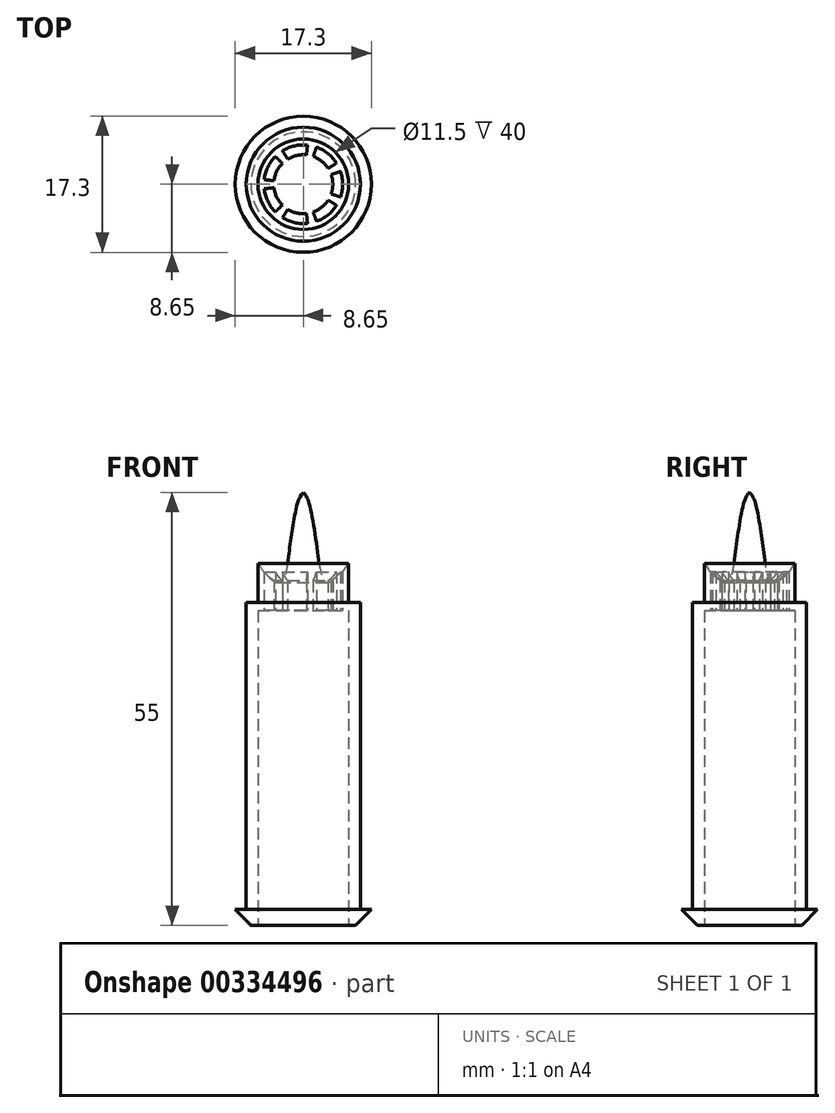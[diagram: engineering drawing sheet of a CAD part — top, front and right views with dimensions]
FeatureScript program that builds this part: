
annotation { "Feature Type Name" : "Feature", "Feature Type Description" : "" }
export const myFeature = defineFeature(function(context is Context, id is Id, definition is map)
    precondition{}
    {
        {
            var Q0;
            Q0=qCreatedBy(makeId("Front.planeOp"),FACE);
            var sketch = newSketch(context, id + "F0", { "sketchPlane" : qUnion([Q0])});
            skLineSegment(sketch, "E0", {"start": v(0, 0) * mm, "end": v(0, 55.6) * mm});
            skLineSegment(sketch, "E1.0", {"start": v(7.25, 2) * mm, "end": v(7.25, 41) * mm});
            skLineSegment(sketch, "E2.0", {"start": v(5.75, 5) * mm, "end": v(5.75, 38) * mm});
            skLineSegment(sketch, "E3.0", {"start": v(8.65, 0) * mm, "end": v(8.65, 2) * mm});
            skLineSegment(sketch, "E4.0", {"start": v(7.25, 2) * mm, "end": v(8.65, 2) * mm});
            skLineSegment(sketch, "E5", {"start": v(5.75, 0) * mm, "end": v(8.65, 0) * mm});
            skLineSegment(sketch, "E6.0", {"start": v(4.75, 40) * mm, "end": v(5.75, 40) * mm});
            skArc(sketch, "E7", {"start": v(5.75, 38) * mm, "mid": v(5.46, 38.7) * mm, "end": v(4.75, 39) * mm});
            skLineSegment(sketch, "E8.trimOffspring", {"start": v(5.75, 40) * mm, "end": v(5.75, 41) * mm});
            skLineSegment(sketch, "E9", {"start": v(4.75, 40) * mm, "end": v(4.75, 39) * mm});
            skPoint(sketch, "E10.endSnap0", {"position": v(5.75, 21.5) * mm});
            skLineSegment(sketch, "E11.MirrorCS", {"start": v(4.75, 3) * mm, "end": v(5.75, 3) * mm});
            skLineSegment(sketch, "E12.MirrorCS", {"start": v(4.75, 3) * mm, "end": v(4.75, 4) * mm});
            skArc(sketch, "E13.MirrorCS", {"start": v(5.75, 5) * mm, "mid": v(5.46, 4.3) * mm, "end": v(4.75, 4) * mm});
            skLineSegment(sketch, "E14", {"start": v(5.75, 3) * mm, "end": v(5.75, 0) * mm});
            skLineSegment(sketch, "E15.0", {"start": v(5.75, 41) * mm, "end": v(7.25, 41) * mm});
            skSolve(sketch);
        }
        {
            var Q0;
            Q0=qSketchRegion(id+"F0",true);
            var Q1;
            Q1=sQuery(id+"F0.wireOp",EDGE,"E0");
            revolve(context, id + "F1", {"entities" : qUnion([Q0]), "axis" : qUnion([Q1]), "revolveType" : RevolveType.FULL});
        }
        {
            var Q0;
            Q0=makeQuery(id+"F1.opRevolve","SWEPT_EDGE",EDGE,{"disambiguationData":[OSD([sQuery(id+"F0.wireOp",EDGE,"E3.0"),sQuery(id+"F0.wireOp",EDGE,"E5")])]});
            chamfer(context, id + "F2", {"entities" : qUnion([Q0]), "chamferType" : ChamferType.TWO_OFFSETS, "width1" : 2 * mm, "oppositeDirection" : false, "width2" : 2 * mm, "tangentPropagation" : true});
        }
        {
            var Q0;
            Q0=qCreatedBy(makeId("Front.planeOp"),FACE);
            var sketch = newSketch(context, id + "F3", { "sketchPlane" : qUnion([Q0])});
            skLineSegment(sketch, "E16", {"start": v(0, 41) * mm, "end": v(0, 55) * mm});
            skLineSegment(sketch, "E17", {"start": v(5.75, 40) * mm, "end": v(5.75, 46) * mm});
            skFitSpline(sketch, "E18", {"points": [v(0, 55) * mm, v(0.35, 54.58) * mm, v(0.8, 53.42) * mm, v(1.77, 47.7) * mm, v(2.42, 44.16) * mm, v(3.02, 43.55) * mm, v(4.25, 44.14) * mm, v(5.17, 45.15) * mm, v(5.75, 46) * mm], "startDerivative": vector(6.12, -4.44) * mm, "endDerivative": vector(6.63, 7.2) * mm});
            skLineSegment(sketch, "E19.0.0", {"start": v(-5.75, 40) * mm, "end": v(5.75, 40) * mm});
            skLineSegment(sketch, "E20", {"start": v(0, 41) * mm, "end": v(0, 39.56) * mm});
            skPoint(sketch, "E20.endSnap0", {"position": v(0, 40) * mm});
            skPoint(sketch, "E21.orphan", {"position": v(5.75, 41) * mm});
            skSolve(sketch);
        }
        {
            var Q0;
            Q0 = qSketchRegion(id + "F3", true);
            var Q1;
            Q1=makeQuery(id+"F1.opRevolve","SWEPT_FACE",FACE,{"disambiguationData":[OSD([sQuery(id+"F0.wireOp",EDGE,"E1.0")])]});
            revolve(context, id + "F4", {"operationType" : NewBodyOperationType.ADD, "surfaceOperationType" : NewSurfaceOperationType.NEW, "entities" : qUnion([Q0]), "axis" : qUnion([Q1]), "revolveType" : RevolveType.FULL});
        }
        {
            var Q0;
            Q0=makeQuery(id+"F4.opRevolve","SWEPT_FACE",FACE,{"disambiguationData":[OSD([sQuery(id+"F3.wireOp",EDGE,"E19.0.0")])]});
            var sketch = newSketch(context, id + "F5", { "sketchPlane" : qUnion([Q0])});
            skCircle(sketch, "E22.0", {"center": v(0, 0) * mm, "radius": 5.75 * mm});
            skSolve(sketch);
        }
        {
            var Q0;
            Q0 = qSketchRegion(id + "F5", true);
            extrude(context, id + "F6", {"entities" : qUnion([Q0]), "operationType" : NewBodyOperationType.REMOVE, "depth" : 25 * mm, "offsetDistance" : 25 * mm});
        }
        {
            var Q0;
            Q0=makeQuery(id+"F1.opRevolve","SWEPT_FACE",FACE,{"disambiguationData":[OSD([sQuery(id+"F0.wireOp",EDGE,"E11.MirrorCS")])]});
            var sketch = newSketch(context, id + "F7", { "sketchPlane" : qUnion([Q0])});
            skCircle(sketch, "E23.0", {"center": v(0, 0) * mm, "radius": 5.75 * mm});
            skSolve(sketch);
        }
        {
            var Q0;
            Q0 = qSketchRegion(id + "F7", true);
            extrude(context, id + "F8", {"entities" : qUnion([Q0]), "operationType" : NewBodyOperationType.REMOVE, "oppositeDirection" : true, "depth" : 25 * mm, "offsetDistance" : 25 * mm});
        }
        {
            var Q0;
            Q0=makeQuery(id+"F6.boolean.opBoolean","MERGE",FACE,{"derivedFrom":[makeQuery(id+"F4.opRevolve","SWEPT_FACE",FACE,{"disambiguationData":[OSD([sQuery(id+"F3.wireOp",EDGE,"E19.0.0")])]}),makeQuery(id+"F6.opExtrude","CAP_FACE",FACE,{"disambiguationData":[OSD([sQuery(id+"F5.wireOp",EDGE,"E22.0")])],"isStart":true})]});
            var sketch = newSketch(context, id + "F9", { "sketchPlane" : qUnion([Q0])});
            skArc(sketch, "E24", {"start": v(3.55, -1.22) * mm, "mid": v(3.75, 0) * mm, "end": v(3.55, 1.22) * mm});
            skArc(sketch, "E25", {"start": v(4.73, -1.63) * mm, "mid": v(5, 0) * mm, "end": v(4.73, 1.63) * mm});
            skLineSegment(sketch, "E26", {"start": v(3.55, 1.22) * mm, "end": v(4.73, 1.63) * mm});
            skLineSegment(sketch, "E27.MirrorCS", {"start": v(3.55, -1.22) * mm, "end": v(4.73, -1.63) * mm});
            skArc(sketch, "E28.1.0", {"start": v(4.22, 2.68) * mm, "mid": v(3.12, 3.9) * mm, "end": v(1.67, 4.71) * mm});
            skLineSegment(sketch, "E28.1.1", {"start": v(3.17, 2) * mm, "end": v(4.22, 2.68) * mm});
            skArc(sketch, "E28.1.2", {"start": v(3.17, 2) * mm, "mid": v(2.34, 2.93) * mm, "end": v(1.26, 3.53) * mm});
            skLineSegment(sketch, "E28.1.3", {"start": v(1.26, 3.53) * mm, "end": v(1.67, 4.71) * mm});
            skArc(sketch, "E28.2.0", {"start": v(0.54, 4.97) * mm, "mid": v(-1.11, 4.87) * mm, "end": v(-2.64, 4.25) * mm});
            skLineSegment(sketch, "E28.2.1", {"start": v(0.4, 3.73) * mm, "end": v(0.54, 4.97) * mm});
            skArc(sketch, "E28.2.2", {"start": v(0.4, 3.73) * mm, "mid": v(-0.83, 3.66) * mm, "end": v(-1.98, 3.18) * mm});
            skLineSegment(sketch, "E28.2.3", {"start": v(-1.98, 3.18) * mm, "end": v(-2.64, 4.25) * mm});
            skArc(sketch, "E28.3.0", {"start": v(-3.55, 3.52) * mm, "mid": v(-4.5, 2.17) * mm, "end": v(-4.97, 0.58) * mm});
            skLineSegment(sketch, "E28.3.1", {"start": v(-2.66, 2.64) * mm, "end": v(-3.55, 3.52) * mm});
            skArc(sketch, "E28.3.2", {"start": v(-2.66, 2.64) * mm, "mid": v(-3.38, 1.63) * mm, "end": v(-3.72, 0.44) * mm});
            skLineSegment(sketch, "E28.3.3", {"start": v(-3.72, 0.44) * mm, "end": v(-4.97, 0.58) * mm});
            skArc(sketch, "E28.4.0", {"start": v(-4.97, -0.58) * mm, "mid": v(-4.5, -2.17) * mm, "end": v(-3.55, -3.52) * mm});
            skLineSegment(sketch, "E28.4.1", {"start": v(-3.72, -0.44) * mm, "end": v(-4.97, -0.58) * mm});
            skArc(sketch, "E28.4.2", {"start": v(-3.72, -0.44) * mm, "mid": v(-3.38, -1.63) * mm, "end": v(-2.66, -2.64) * mm});
            skLineSegment(sketch, "E28.4.3", {"start": v(-2.66, -2.64) * mm, "end": v(-3.55, -3.52) * mm});
            skArc(sketch, "E28.5.0", {"start": v(-2.64, -4.25) * mm, "mid": v(-1.11, -4.87) * mm, "end": v(0.54, -4.97) * mm});
            skLineSegment(sketch, "E28.5.1", {"start": v(-1.98, -3.18) * mm, "end": v(-2.64, -4.25) * mm});
            skArc(sketch, "E28.5.2", {"start": v(-1.98, -3.18) * mm, "mid": v(-0.83, -3.66) * mm, "end": v(0.4, -3.73) * mm});
            skLineSegment(sketch, "E28.5.3", {"start": v(0.4, -3.73) * mm, "end": v(0.54, -4.97) * mm});
            skArc(sketch, "E28.6.0", {"start": v(1.67, -4.71) * mm, "mid": v(3.12, -3.9) * mm, "end": v(4.22, -2.68) * mm});
            skLineSegment(sketch, "E28.6.1", {"start": v(1.26, -3.53) * mm, "end": v(1.67, -4.71) * mm});
            skArc(sketch, "E28.6.2", {"start": v(1.26, -3.53) * mm, "mid": v(2.34, -2.93) * mm, "end": v(3.17, -2) * mm});
            skLineSegment(sketch, "E28.6.3", {"start": v(3.17, -2) * mm, "end": v(4.22, -2.68) * mm});
            skSolve(sketch);
        }
        {
            var Q0;
            Q0 = qSketchRegion(id + "F9", true);
            extrude(context, id + "F10", {"entities" : qUnion([Q0]), "operationType" : NewBodyOperationType.REMOVE, "oppositeDirection" : true, "depth" : 25 * mm, "offsetDistance" : 25 * mm});
        }
    });
